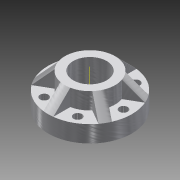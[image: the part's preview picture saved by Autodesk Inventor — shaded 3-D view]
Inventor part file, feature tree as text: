
AUTODESK INVENTOR PART (.ipt)
format: ipt  version: 2015 (Build 190159000, 159)  size: 179,200 bytes
history: native  units: in
note: dims shown in document units (in); Inventor stores cm internally (conversion verified against a paired STEP export)
features: sketch x4, extrude x3, other x2, pattern_circular x2, hole x1, chamfer x1
ambient origin geometry x8: Origin, YZ Plane, XZ Plane, XY Plane, X Axis, Y Axis, Z Axis, Center Point
bodies: Body1 (feature_tree)
feature tree (13):
  other  "pegg"
  extrude  "Extrusion1"  Depth=2.5in
  extrude  "Extrusion2"  Depth=1.5in
  hole  "Hole1"  [1 undecoded]
  other  "Work Axis1"
  pattern_circular  "Circular Pattern1"  [2 undecoded]
  extrude  "Extrusion3"  Depth=0.75in TaperAngle=45.0deg
  chamfer  "Chamfer1"  Distance=2.3622in Angle=360.0deg
  pattern_circular  "Circular Pattern2"  [2 undecoded]
  sketch  "Sketch1"  dims[d0=1.0in d1=2.5in]
  sketch  "Sketch2"  dims[d3=0.5in d4=0.0in d5=1.5in]
  sketch  "Sketch3"  dims[d6=0.5in d7=0.0in]
  sketch  "Sketch4"  dims[d8=0.25in d9=0.75in d10=0.375in d11=0.25in d12=0.5635in d13=1.0in d14=0.8108in d15=2.3622in d16=360.0deg d20=0.5in d21=0.0in d22=0.5in d23=0.125in d24=45.0deg d25=2.3622in d26=360.0deg]
note: 5 required parameter values undecoded (feature->parameter linkage not recoverable at this tier; creation-order binding heuristic only, values carry confidence <= 0.55)
